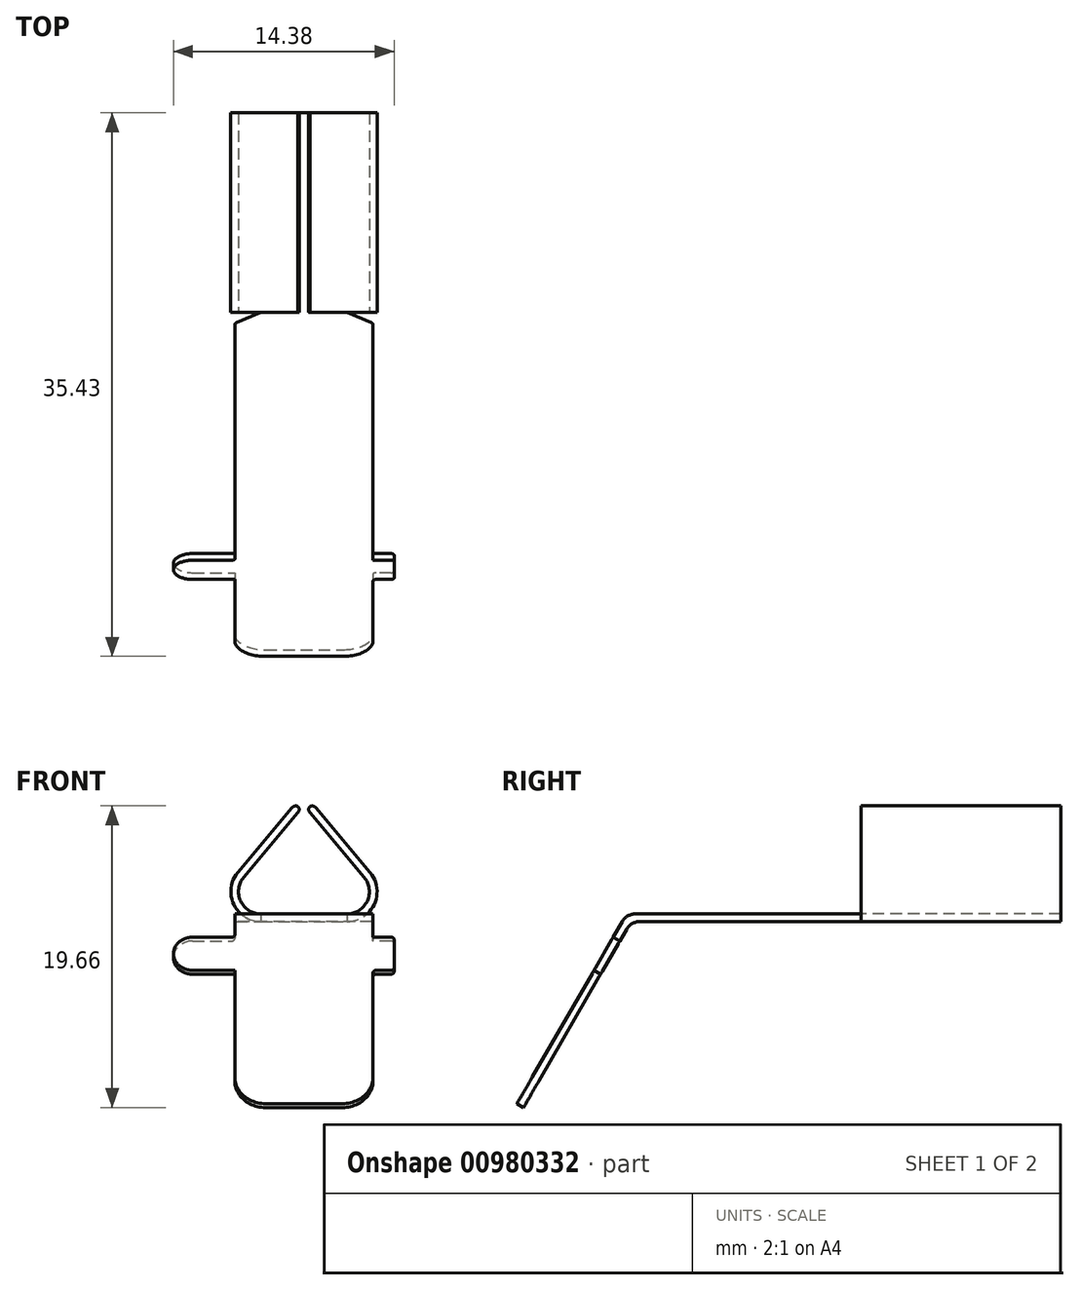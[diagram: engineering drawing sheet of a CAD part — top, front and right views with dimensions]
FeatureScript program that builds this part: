
annotation { "Feature Type Name" : "Feature", "Feature Type Description" : "" }
export const myFeature = defineFeature(function(context is Context, id is Id, definition is map)
    precondition{}
    {
        {
            var Q0;
            Q0=qCreatedBy(makeId("Front.planeOp"),FACE);
            var sketch = newSketch(context, id + "F0", { "sketchPlane" : qUnion([Q0])});
            skLineSegment(sketch, "E0", {"start": v(-0.57, 7.66) * mm, "end": v(-4.3, 3.2) * mm});
            skLineSegment(sketch, "E1", {"start": v(-2.81, 0) * mm, "end": v(0, 0) * mm});
            skLineSegment(sketch, "E2", {"start": v(0, 0.5) * mm, "end": v(-2.81, 0.5) * mm});
            skLineSegment(sketch, "E3", {"start": v(-3.92, 2.89) * mm, "end": v(-0.19, 7.34) * mm});
            skLineSegment(sketch, "E4", {"start": v(-0.19, 7.34) * mm, "end": v(-0.57, 7.66) * mm});
            skLineSegment(sketch, "E5", {"start": v(0, 4.01) * mm, "end": v(0, -0.67) * mm, "construction": true});
            skLineSegment(sketch, "E6", {"start": v(0, 0.5) * mm, "end": v(0, 0) * mm});
            skPoint(sketch, "E7.visualSharp", {"position": v(-7, 0) * mm});
            skLineSegment(sketch, "E8.filletArc", {"start": v(-6.38, 0.74) * mm, "end": v(-6.38, 0.74) * mm});
            skArc(sketch, "E9.filletArc", {"start": v(-3.92, 2.89) * mm, "mid": v(-4.13, 1.34) * mm, "end": v(-2.81, 0.5) * mm});
            skArc(sketch, "E10.filletArc", {"start": v(-4.3, 3.2) * mm, "mid": v(-4.58, 1.13) * mm, "end": v(-2.81, 0) * mm});
            skLineSegment(sketch, "E11.MirrorCS", {"start": v(0.19, 7.34) * mm, "end": v(0.57, 7.66) * mm});
            skLineSegment(sketch, "E12.MirrorCS", {"start": v(2.81, 0) * mm, "end": v(0, 0) * mm});
            skArc(sketch, "E13.MirrorCS", {"start": v(3.92, 2.89) * mm, "mid": v(4.13, 1.34) * mm, "end": v(2.81, 0.5) * mm});
            skLineSegment(sketch, "E14.MirrorCS", {"start": v(3.92, 2.89) * mm, "end": v(0.19, 7.34) * mm});
            skArc(sketch, "E15.MirrorCS", {"start": v(4.3, 3.2) * mm, "mid": v(4.58, 1.13) * mm, "end": v(2.81, 0) * mm});
            skLineSegment(sketch, "E16.MirrorCS", {"start": v(0.57, 7.66) * mm, "end": v(4.3, 3.2) * mm});
            skLineSegment(sketch, "E17.MirrorCS", {"start": v(0, 0.5) * mm, "end": v(2.81, 0.5) * mm});
            skLineSegment(sketch, "E18", {"start": v(-4.76, 3.82) * mm, "end": v(-4.76, 0) * mm, "construction": true});
            skLineSegment(sketch, "E19", {"start": v(4.76, 4.24) * mm, "end": v(4.76, 0) * mm, "construction": true});
            skSolve(sketch);
        }
        {
            var Q0;
            Q0 = qSketchRegion(id + "F0", true);
            extrude(context, id + "F1", {"entities" : qUnion([Q0]), "oppositeDirection" : true, "depth" : 13 * mm, "offsetDistance" : 25 * mm});
        }
        {
            var Q0;
            Q0=makeQuery(id+"F1.opExtrude","SWEPT_FACE",FACE,{"disambiguationData":[OSD([sQuery(id+"F0.wireOp",EDGE,"E1"),sQuery(id+"F0.wireOp",EDGE,"E12.MirrorCS")])]});
            cPlane(context, id + "F2", {"entities" : qUnion([Q0]), "cplaneType" : CPlaneType.OFFSET, "offset" : 0 * mm, "width" : 150 * mm, "height" : 150 * mm});
        }
        {
            var Q0;
            Q0=qCreatedBy(id+"F2.planeOp",FACE);
            var sketch = newSketch(context, id + "F3", { "sketchPlane" : qUnion([Q0])});
            skLineSegment(sketch, "E20.0.0", {"start": v(2.81, 0) * mm, "end": v(-2.81, 0) * mm});
            skLineSegment(sketch, "E20.0.1", {"start": v(-2.81, 0) * mm, "end": v(-2.81, -13) * mm});
            skLineSegment(sketch, "E20.0.2", {"start": v(-2.81, -13) * mm, "end": v(2.81, -13) * mm});
            skLineSegment(sketch, "E20.0.3", {"start": v(2.81, -13) * mm, "end": v(2.81, 0) * mm});
            skLineSegment(sketch, "E21", {"start": v(4.5, 15) * mm, "end": v(-4.5, 15) * mm});
            skLineSegment(sketch, "E22", {"start": v(-4.5, 15) * mm, "end": v(-4.5, 0.82) * mm});
            skLineSegment(sketch, "E23", {"start": v(0, 0) * mm, "end": v(0, 0) * mm});
            skLineSegment(sketch, "E24", {"start": v(-2.81, 0) * mm, "end": v(2.81, 0) * mm});
            skLineSegment(sketch, "E25", {"start": v(0, 0) * mm, "end": v(0, 17.66) * mm, "construction": true});
            skLineSegment(sketch, "E26", {"start": v(4.5, 0.82) * mm, "end": v(4.5, 15) * mm});
            skLineSegment(sketch, "E27", {"start": v(-4.4, 0.68) * mm, "end": v(-2.81, 0) * mm});
            skLineSegment(sketch, "E28", {"start": v(4.4, 0.68) * mm, "end": v(2.81, 0) * mm});
            skPoint(sketch, "E29.visualSharp", {"position": v(-4.5, 0.72) * mm});
            skArc(sketch, "E29.filletArc", {"start": v(-4.5, 0.82) * mm, "mid": v(-4.47, 0.74) * mm, "end": v(-4.4, 0.68) * mm});
            skPoint(sketch, "E30.visualSharp", {"position": v(4.5, 0.72) * mm});
            skArc(sketch, "E30.filletArc", {"start": v(4.4, 0.68) * mm, "mid": v(4.47, 0.74) * mm, "end": v(4.5, 0.82) * mm});
            skSolve(sketch);
        }
        {
            var Q0;
            Q0 = qSketchRegion(id + "F3", true);
            var Q1;
            Q1=makeQuery(id+"F1.opExtrude","SWEPT_FACE",FACE,{"disambiguationData":[OSD([sQuery(id+"F0.wireOp",EDGE,"E2"),sQuery(id+"F0.wireOp",EDGE,"E17.MirrorCS")])]});
            extrude(context, id + "F4", {"entities" : qUnion([Q0]), "operationType" : NewBodyOperationType.ADD, "endBound" : BoundingType.UP_TO_SURFACE, "oppositeDirection" : true, "depth" : 0.5 * mm, "endBoundEntityFace" : qUnion([Q1]), "offsetDistance" : 25 * mm});
        }
        {
            var Q0;
            Q0=makeQuery(id+"F4.opExtrude","SWEPT_FACE",FACE,{"disambiguationData":[OSD([sQuery(id+"F3.wireOp",EDGE,"E26")])]});
            var sketch = newSketch(context, id + "F5", { "sketchPlane" : qUnion([Q0])});
            skLineSegment(sketch, "E31.MirrorCS", {"start": v(-22, -12.12) * mm, "end": v(-22.43, -11.87) * mm});
            skLineSegment(sketch, "E32.MirrorCS", {"start": v(-15.29, 0.5) * mm, "end": v(-15, 0.5) * mm});
            skLineSegment(sketch, "E33.MirrorCS", {"start": v(-15, 0) * mm, "end": v(-22, -12.12) * mm});
            skLineSegment(sketch, "E34.MirrorCS", {"start": v(-22.43, -11.87) * mm, "end": v(-15.29, 0.5) * mm});
            skSolve(sketch);
        }
        {
            var Q0;
            Q0=makeQuery(id+"F5.imprint","IMPRINT",FACE,{"disambiguationData":[TD([[makeQuery(id+"F5.imprint","IMPRINT",EDGE,{"derivedFrom":sQuery(id+"F5.wireOp",EDGE,"E31.MirrorCS")}),-1.0]])]});
            var Q1;
            Q1=makeQuery(id+"F4.opExtrude","SWEPT_FACE",FACE,{"disambiguationData":[OSD([sQuery(id+"F3.wireOp",EDGE,"E22")])]});
            extrude(context, id + "F6", {"entities" : qUnion([Q0]), "operationType" : NewBodyOperationType.ADD, "endBound" : BoundingType.UP_TO_SURFACE, "oppositeDirection" : true, "depth" : 25 * mm, "endBoundEntityFace" : qUnion([Q1]), "offsetDistance" : 25 * mm});
        }
        {
            var Q0;
            Q0=makeQuery(id+"F6.opExtrude","SWEPT_FACE",FACE,{"disambiguationData":[OSD([sQuery(id+"F5.wireOp",EDGE,"E34.MirrorCS")])]});
            cPlane(context, id + "F7", {"entities" : qUnion([Q0]), "cplaneType" : CPlaneType.OFFSET, "offset" : 0 * mm, "width" : 150 * mm, "height" : 150 * mm});
        }
        {
            var Q0;
            Q0=qCreatedBy(id+"F7.planeOp",FACE);
            var sketch = newSketch(context, id + "F8", { "sketchPlane" : qUnion([Q0])});
            skLineSegment(sketch, "E35.0.0", {"start": v(-4.5, -7.21) * mm, "end": v(-4.5, -21.5) * mm});
            skLineSegment(sketch, "E35.0.1", {"start": v(-4.5, -21.5) * mm, "end": v(4.5, -21.5) * mm});
            skLineSegment(sketch, "E35.0.2", {"start": v(4.5, -21.5) * mm, "end": v(4.5, -11.46) * mm});
            skLineSegment(sketch, "E35.0.3", {"start": v(4.5, -7.21) * mm, "end": v(-4.5, -7.21) * mm});
            skPoint(sketch, "E36.0", {"position": v(0, 0) * mm});
            skLineSegment(sketch, "E37", {"start": v(0, -5.66) * mm, "end": v(0, -24.45) * mm, "construction": true});
            skLineSegment(sketch, "E38", {"start": v(-5.47, -10.21) * mm, "end": v(6.35, -10.21) * mm, "construction": true});
            skLineSegment(sketch, "E39", {"start": v(4.5, -11.46) * mm, "end": v(7.25, -11.46) * mm});
            skLineSegment(sketch, "E40.MirrorCS", {"start": v(4.5, -8.96) * mm, "end": v(7.25, -8.96) * mm});
            skArc(sketch, "E41", {"start": v(7.25, -8.96) * mm, "mid": v(8.5, -10.21) * mm, "end": v(7.25, -11.46) * mm});
            skPoint(sketch, "E42", {"position": v(8.5, -10.21) * mm});
            skLineSegment(sketch, "E43.trimOffspring", {"start": v(4.5, -8.96) * mm, "end": v(4.5, -7.21) * mm});
            skLineSegment(sketch, "E44.MirrorCS", {"start": v(4.5, -13.21) * mm, "end": v(-4.5, -13.21) * mm});
            skArc(sketch, "E45.MirrorCS", {"start": v(7.25, -11.46) * mm, "mid": v(8.5, -10.21) * mm, "end": v(7.25, -8.96) * mm});
            skLineSegment(sketch, "E46.MirrorCS", {"start": v(4.5, -11.46) * mm, "end": v(4.5, -13.21) * mm});
            skLineSegment(sketch, "E47.MirrorCS", {"start": v(4.5, 1.08) * mm, "end": v(4.5, -8.96) * mm});
            skLineSegment(sketch, "E48.MirrorCS", {"start": v(0, -14.76) * mm, "end": v(0, 4.02) * mm, "construction": true});
            skLineSegment(sketch, "E49.MirrorCS", {"start": v(-4.5, -8.96) * mm, "end": v(-7.25, -8.96) * mm});
            skLineSegment(sketch, "E50.MirrorCS", {"start": v(-4.5, -11.46) * mm, "end": v(-7.25, -11.46) * mm});
            skPoint(sketch, "E51.MirrorP", {"position": v(-8.5, -10.21) * mm});
            skArc(sketch, "E52.MirrorCS", {"start": v(-7.25, -8.96) * mm, "mid": v(-8.5, -10.21) * mm, "end": v(-7.25, -11.46) * mm});
            skArc(sketch, "E53.MirrorCS", {"start": v(-7.25, -11.46) * mm, "mid": v(-8.5, -10.21) * mm, "end": v(-7.25, -8.96) * mm});
            skLineSegment(sketch, "E54", {"start": v(5.88, -8.96) * mm, "end": v(5.88, -11.46) * mm});
            skLineSegment(sketch, "E55", {"start": v(-5.88, -8.96) * mm, "end": v(-5.88, -11.46) * mm});
            skSolve(sketch);
        }
        {
            var Q0;
            {var subQ0=sQuery(id+"F8.wireOp",EDGE,"E49.MirrorCS");Q0=makeQuery(id+"F8.imprint","IMPRINT",FACE,{"disambiguationData":[TD([[makeQuery(id+"F8.imprint","IMPRINT",EDGE,{"derivedFrom":subQ0}),1.0]])]});}
            var Q1;
            {var subQ3=sQuery(id+"F8.wireOp",EDGE,"E35.0.3");Q1=makeQuery(id+"F8.imprint","IMPRINT",FACE,{"disambiguationData":[TD([[makeQuery(id+"F8.imprint","IMPRINT",EDGE,{"derivedFrom":subQ3}),1.0]])]});}
            var Q2;
            {var subQ0=sQuery(id+"F8.wireOp",EDGE,"E45.MirrorCS");Q2=makeQuery(id+"F8.imprint","IMPRINT",FACE,{"disambiguationData":[TD([[makeQuery(id+"F8.imprint","IMPRINT",EDGE,{"derivedFrom":subQ0}),1.0]])]});}
            var Q3;
            Q3=makeQuery(id+"F6.opExtrude","SWEPT_FACE",FACE,{"disambiguationData":[OSD([sQuery(id+"F5.wireOp",EDGE,"E33.MirrorCS")])]});
            extrude(context, id + "F9", {"entities" : qUnion([Q0, Q1, Q2]), "operationType" : NewBodyOperationType.ADD, "endBound" : BoundingType.UP_TO_SURFACE, "oppositeDirection" : true, "depth" : 25 * mm, "endBoundEntityFace" : qUnion([Q3]), "offsetDistance" : 25 * mm});
        }
        {
            var Q0;
            Q0=makeQuery(id+"F6.opExtrude","CAP_EDGE",EDGE,{"disambiguationData":[OSD([sQuery(id+"F5.wireOp",EDGE,"E31.MirrorCS")])],"isStart":true});
            var Q1;
            Q1=makeQuery(id+"F6.opExtrude","CAP_EDGE",EDGE,{"disambiguationData":[OSD([sQuery(id+"F5.wireOp",EDGE,"E31.MirrorCS")])],"isStart":false});
            fillet(context, id + "F10", {"entities" : qUnion([Q0, Q1]), "radius" : 2 * mm, "tangentPropagation" : true, "allowEdgeOverflow" : false});
        }
        {
            var Q0;
            Q0=makeQuery(id+"F6.opExtrude","SWEPT_EDGE",EDGE,{"disambiguationData":[OSD([sQuery(id+"F5.wireOp",EDGE,"E32.MirrorCS"),sQuery(id+"F5.wireOp",EDGE,"E34.MirrorCS")])]});
            var Q1;
            {var subQ0=sQuery(id+"F3.wireOp",EDGE,"E21");Q1=makeQuery(id+"F6.boolean.opBoolean","MERGE",EDGE,{"derivedFrom":[makeQuery(id+"F4.opExtrude","CAP_EDGE",EDGE,{"disambiguationData":[OSD([subQ0])],"isStart":true}),makeQuery(id+"F6.opExtrude","SWEPT_EDGE",EDGE,{"disambiguationData":[OSD([sQuery(id+"F3.wireOp",EDGE,"nP5q9VTg-kr94-Q3Wm-ByjT-hHxJVp7QYcDy"),subQ0,sQuery(id+"F5.wireOp",EDGE,"E33.MirrorCS")])]})]});}
            fillet(context, id + "F11", {"entities" : qUnion([Q0, Q1]), "radius" : 1 * mm, "tangentPropagation" : true, "allowEdgeOverflow" : false});
        }
        {
            var Q0;
            Q0=makeQuery(id+"F1.opExtrude","SWEPT_EDGE",EDGE,{"disambiguationData":[OSD([sQuery(id+"F0.wireOp",EDGE,"E11.MirrorCS"),sQuery(id+"F0.wireOp",EDGE,"E14.MirrorCS")])]});
            var Q1;
            Q1=makeQuery(id+"F1.opExtrude","SWEPT_EDGE",EDGE,{"disambiguationData":[OSD([sQuery(id+"F0.wireOp",EDGE,"E3"),sQuery(id+"F0.wireOp",EDGE,"E4")])]});
            var Q2;
            Q2=makeQuery(id+"F1.opExtrude","SWEPT_EDGE",EDGE,{"disambiguationData":[OSD([sQuery(id+"F0.wireOp",EDGE,"E11.MirrorCS"),sQuery(id+"F0.wireOp",EDGE,"E16.MirrorCS")])]});
            var Q3;
            Q3=makeQuery(id+"F1.opExtrude","SWEPT_EDGE",EDGE,{"disambiguationData":[OSD([sQuery(id+"F0.wireOp",EDGE,"E0"),sQuery(id+"F0.wireOp",EDGE,"E4")])]});
            fillet(context, id + "F12", {"entities" : qUnion([Q0, Q1, Q2, Q3]), "radius" : 0.3 * mm, "tangentPropagation" : true, "allowEdgeOverflow" : false});
        }
        {
            var Q0;
            Q0=makeQuery(id+"F9.opExtrude","SWEPT_EDGE",EDGE,{"disambiguationData":[OSD([sQuery(id+"F8.wireOp",EDGE,"E35.0.0"),sQuery(id+"F8.wireOp",EDGE,"E49.MirrorCS")])]});
            var Q1;
            Q1=makeQuery(id+"F9.opExtrude","SWEPT_EDGE",EDGE,{"disambiguationData":[OSD([sQuery(id+"F8.wireOp",EDGE,"E35.0.0"),sQuery(id+"F8.wireOp",EDGE,"E50.MirrorCS")])]});
            var Q2;
            Q2=makeQuery(id+"F9.opExtrude","SWEPT_EDGE",EDGE,{"disambiguationData":[OSD([sQuery(id+"F8.wireOp",EDGE,"E40.MirrorCS"),sQuery(id+"F8.wireOp",EDGE,"E47.MirrorCS")])]});
            var Q3;
            Q3=makeQuery(id+"F9.opExtrude","SWEPT_EDGE",EDGE,{"disambiguationData":[OSD([sQuery(id+"F8.wireOp",EDGE,"E46.MirrorCS"),sQuery(id+"F8.wireOp",EDGE,"E39")])]});
            var Q4;
            Q4=makeQuery(id+"F4.opExtrude","SWEPT_EDGE",EDGE,{"disambiguationData":[OSD([sQuery(id+"F3.wireOp",EDGE,"E20.0.3"),sQuery(id+"F3.wireOp",EDGE,"E24"),sQuery(id+"F3.wireOp",EDGE,"WCOdVOh2-nmQ0-6xFI-413K-fJzorqBgaG5s")])]});
            var Q5;
            Q5=makeQuery(id+"F4.opExtrude","SWEPT_EDGE",EDGE,{"disambiguationData":[OSD([sQuery(id+"F3.wireOp",EDGE,"E20.0.1"),sQuery(id+"F3.wireOp",EDGE,"E24"),sQuery(id+"F3.wireOp",EDGE,"0NLqXI98-bY8a-zg0F-wmVW-EKjsbuOdz86r")])]});
            fillet(context, id + "F13", {"entities" : qUnion([Q0, Q1, Q2, Q3, Q4, Q5]), "radius" : 0.2 * mm, "tangentPropagation" : true, "allowEdgeOverflow" : false});
        }
    });
